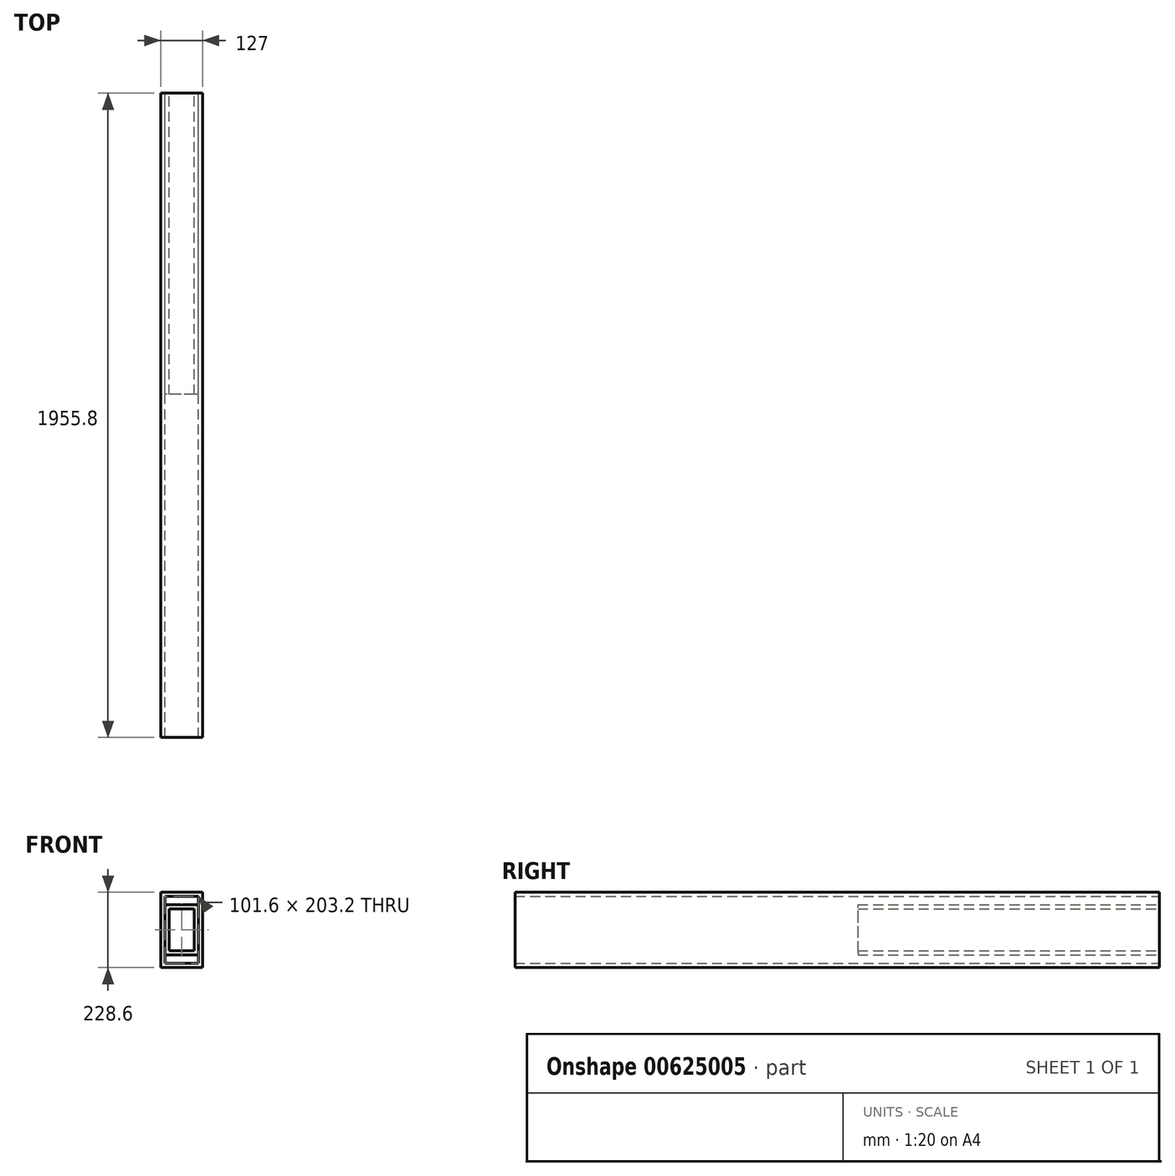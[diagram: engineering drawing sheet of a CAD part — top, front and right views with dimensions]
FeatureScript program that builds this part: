
annotation { "Feature Type Name" : "Feature", "Feature Type Description" : "" }
export const myFeature = defineFeature(function(context is Context, id is Id, definition is map)
    precondition{}
    {
        {
            var Q0;
            Q0=qCreatedBy(makeId("Front.planeOp"),FACE);
            var sketch = newSketch(context, id + "F0", { "sketchPlane" : qUnion([Q0])});
            skLineSegment(sketch, "E0.bottom", {"start": v(50.8, -101.6) * mm, "end": v(-50.8, -101.6) * mm});
            skLineSegment(sketch, "E0.top", {"start": v(50.8, 101.6) * mm, "end": v(-50.8, 101.6) * mm});
            skLineSegment(sketch, "E0.left", {"start": v(50.8, -101.6) * mm, "end": v(50.8, 101.6) * mm});
            skLineSegment(sketch, "E0.right", {"start": v(-50.8, -101.6) * mm, "end": v(-50.8, 101.6) * mm});
            skPoint(sketch, "E0.middle", {"position": v(0, 0) * mm});
            skLineSegment(sketch, "E1.bottom", {"start": v(63.5, -114.3) * mm, "end": v(-63.5, -114.3) * mm});
            skLineSegment(sketch, "E1.top", {"start": v(63.5, 114.3) * mm, "end": v(-63.5, 114.3) * mm});
            skLineSegment(sketch, "E1.left", {"start": v(63.5, -114.3) * mm, "end": v(63.5, 114.3) * mm});
            skLineSegment(sketch, "E1.right", {"start": v(-63.5, -114.3) * mm, "end": v(-63.5, 114.3) * mm});
            skSolve(sketch);
        }
        {
            var Q0;
            Q0 = qSketchRegion(id + "F0", true);
            extrude(context, id + "F1", {"entities" : qUnion([Q0]), "depth" : 1955.8 * mm, "offsetDistance" : 25.4 * mm});
        }
        {
            var Q0;
            Q0=qCreatedBy(makeId("Front.planeOp"),FACE);
            var sketch = newSketch(context, id + "F2", { "sketchPlane" : qUnion([Q0])});
            skLineSegment(sketch, "E2.bottom", {"start": v(44.45, -76.2) * mm, "end": v(-44.45, -76.2) * mm});
            skLineSegment(sketch, "E2.top", {"start": v(44.45, 76.2) * mm, "end": v(-44.45, 76.2) * mm});
            skLineSegment(sketch, "E2.left", {"start": v(50.8, -69.85) * mm, "end": v(50.8, 69.85) * mm});
            skLineSegment(sketch, "E2.right", {"start": v(-50.8, -69.85) * mm, "end": v(-50.8, 69.85) * mm});
            skPoint(sketch, "E2.middle", {"position": v(0, 0) * mm});
            skLineSegment(sketch, "E3.bottom", {"start": v(38.1, -63.5) * mm, "end": v(-38.1, -63.5) * mm});
            skLineSegment(sketch, "E3.top", {"start": v(38.1, 63.5) * mm, "end": v(-38.1, 63.5) * mm});
            skLineSegment(sketch, "E3.left", {"start": v(38.1, -63.5) * mm, "end": v(38.1, 63.5) * mm});
            skLineSegment(sketch, "E3.right", {"start": v(-38.1, -63.5) * mm, "end": v(-38.1, 63.5) * mm});
            skPoint(sketch, "E4.visualSharp", {"position": v(-50.8, 76.2) * mm});
            skArc(sketch, "E4.filletArc", {"start": v(-44.45, 76.2) * mm, "mid": v(-48.94, 74.34) * mm, "end": v(-50.8, 69.85) * mm});
            skPoint(sketch, "E5.visualSharp", {"position": v(50.8, 76.2) * mm});
            skArc(sketch, "E5.filletArc", {"start": v(50.8, 69.85) * mm, "mid": v(48.94, 74.34) * mm, "end": v(44.45, 76.2) * mm});
            skPoint(sketch, "E6.visualSharp", {"position": v(50.8, -76.2) * mm});
            skArc(sketch, "E6.filletArc", {"start": v(44.45, -76.2) * mm, "mid": v(48.94, -74.34) * mm, "end": v(50.8, -69.85) * mm});
            skPoint(sketch, "E7.visualSharp", {"position": v(-50.8, -76.2) * mm});
            skArc(sketch, "E7.filletArc", {"start": v(-50.8, -69.85) * mm, "mid": v(-48.94, -74.34) * mm, "end": v(-44.45, -76.2) * mm});
            skSolve(sketch);
        }
        {
            var Q0;
            Q0 = qSketchRegion(id + "F2", true);
            extrude(context, id + "F3", {"entities" : qUnion([Q0]), "depth" : 914.4 * mm, "offsetDistance" : 25.4 * mm});
        }
    });
